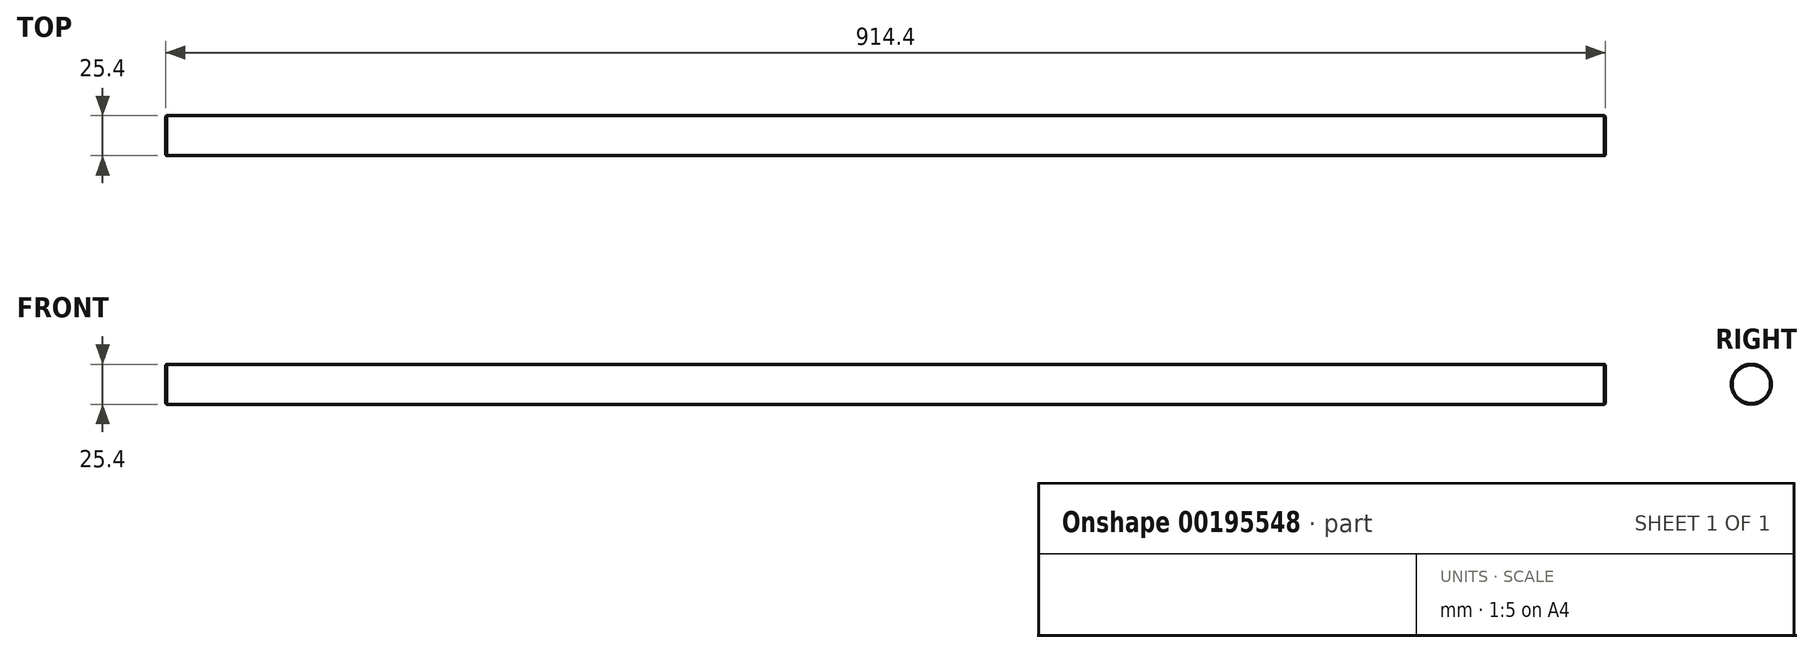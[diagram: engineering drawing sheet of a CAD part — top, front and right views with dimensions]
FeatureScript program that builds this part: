
annotation { "Feature Type Name" : "Feature", "Feature Type Description" : "" }
export const myFeature = defineFeature(function(context is Context, id is Id, definition is map)
    precondition{}
    {
        {
            var Q0;
            Q0=qCreatedBy(makeId("Right.planeOp"),FACE);
            var sketch = newSketch(context, id + "F0", { "sketchPlane" : qUnion([Q0])});
            skCircle(sketch, "E0", {"center": v(0, 0) * mm, "radius": 12.7 * mm});
            skSolve(sketch);
        }
        {
            var Q0;
            Q0=makeQuery(id+"F0.imprint","IMPRINT",FACE,{"disambiguationData":[TD([[makeQuery(id+"F0.imprint","IMPRINT",EDGE,{"derivedFrom":sQuery(id+"F0.wireOp",EDGE,"E0")}),1.0]])]});
            var Q1;
            Q1=sQuery(id+"F0.wireOp",EDGE,"E0");
            extrude(context, id + "F1", {"entities" : qUnion([Q0]), "surfaceEntities" : qUnion([Q1]), "depth" : 914.4 * mm});
        }
        {
            var Q0;
            Q0=makeQuery(id+"F1.opExtrude","CAP_EDGE",EDGE,{"disambiguationData":[OSD([sQuery(id+"F0.wireOp",EDGE,"E0")])],"isStart":false});
            var Q1;
            Q1=makeQuery(id+"F1.opExtrude","CAP_EDGE",EDGE,{"disambiguationData":[OSD([sQuery(id+"F0.wireOp",EDGE,"E0")])],"isStart":true});
            chamfer(context, id + "F2", {"entities" : qUnion([Q0, Q1]), "width" : 0.5 * mm, "tangentPropagation" : true});
        }
    });
